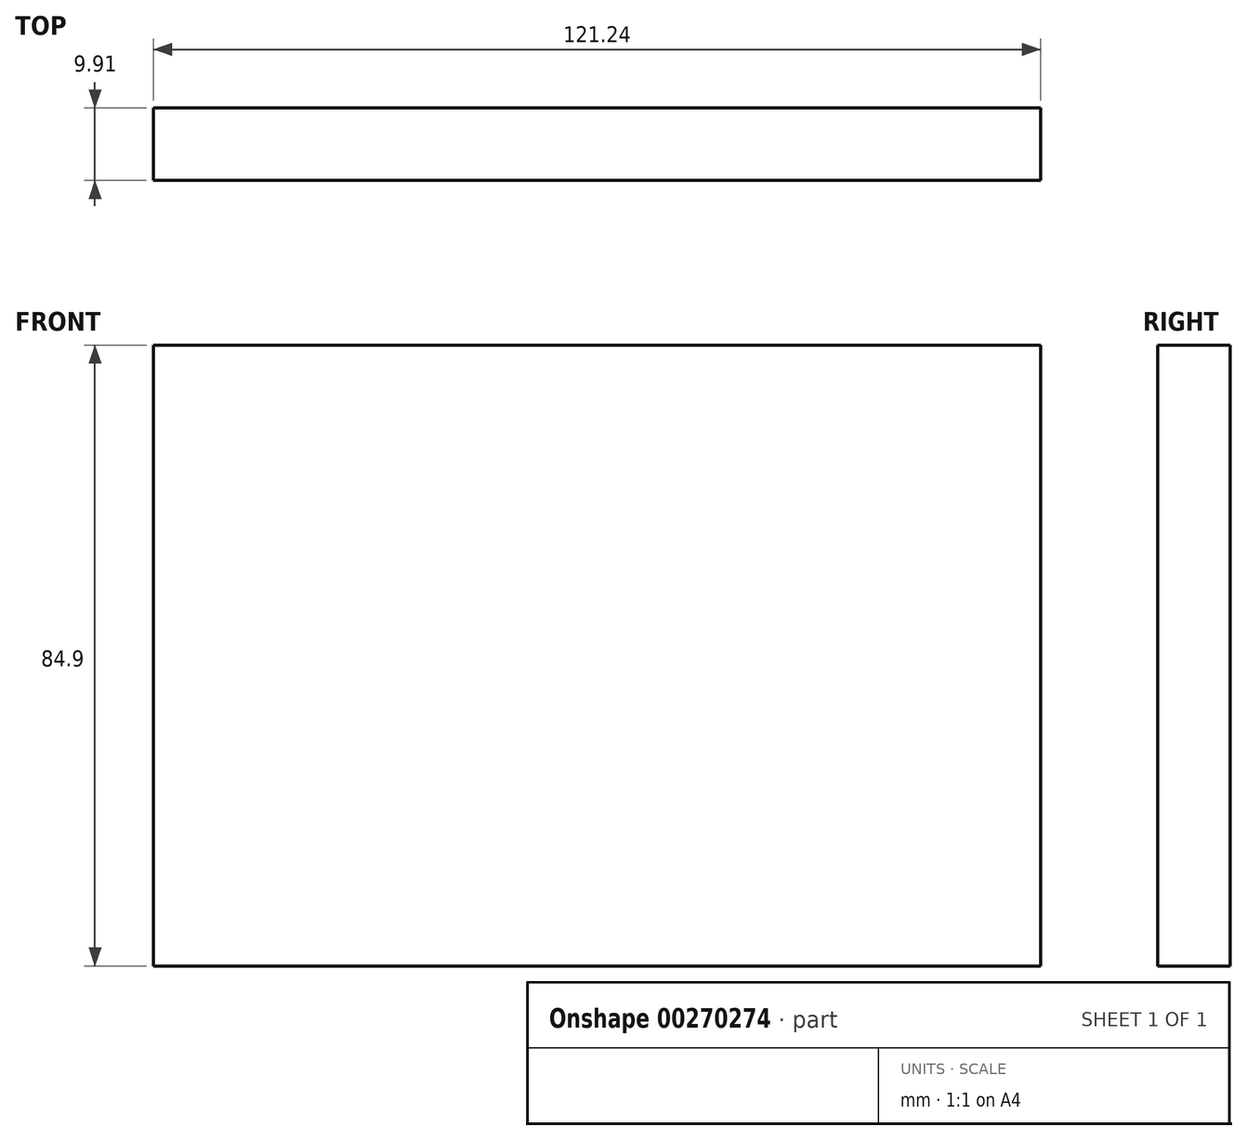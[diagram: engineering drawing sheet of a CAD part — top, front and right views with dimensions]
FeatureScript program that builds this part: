
annotation { "Feature Type Name" : "Feature", "Feature Type Description" : "" }
export const myFeature = defineFeature(function(context is Context, id is Id, definition is map)
    precondition{}
    {
        {
            var Q0;
            Q0=qCreatedBy(makeId("Front.planeOp"),FACE);
            var sketch = newSketch(context, id + "F0", { "sketchPlane" : qUnion([Q0])});
            skLineSegment(sketch, "E0.bottom", {"start": v(-61.12, 53.33) * mm, "end": v(60.12, 53.33) * mm});
            skLineSegment(sketch, "E0.top", {"start": v(-61.12, -31.57) * mm, "end": v(60.12, -31.57) * mm});
            skLineSegment(sketch, "E0.left", {"start": v(-61.12, 53.33) * mm, "end": v(-61.12, -31.57) * mm});
            skLineSegment(sketch, "E0.right", {"start": v(60.12, 53.33) * mm, "end": v(60.12, -31.57) * mm});
            skSolve(sketch);
        }
        {
            var Q0;
            Q0 = qSketchRegion(id + "F0", true);
            extrude(context, id + "F1", {"entities" : qUnion([Q0]), "depth" : 9.9 * mm});
        }
    });
